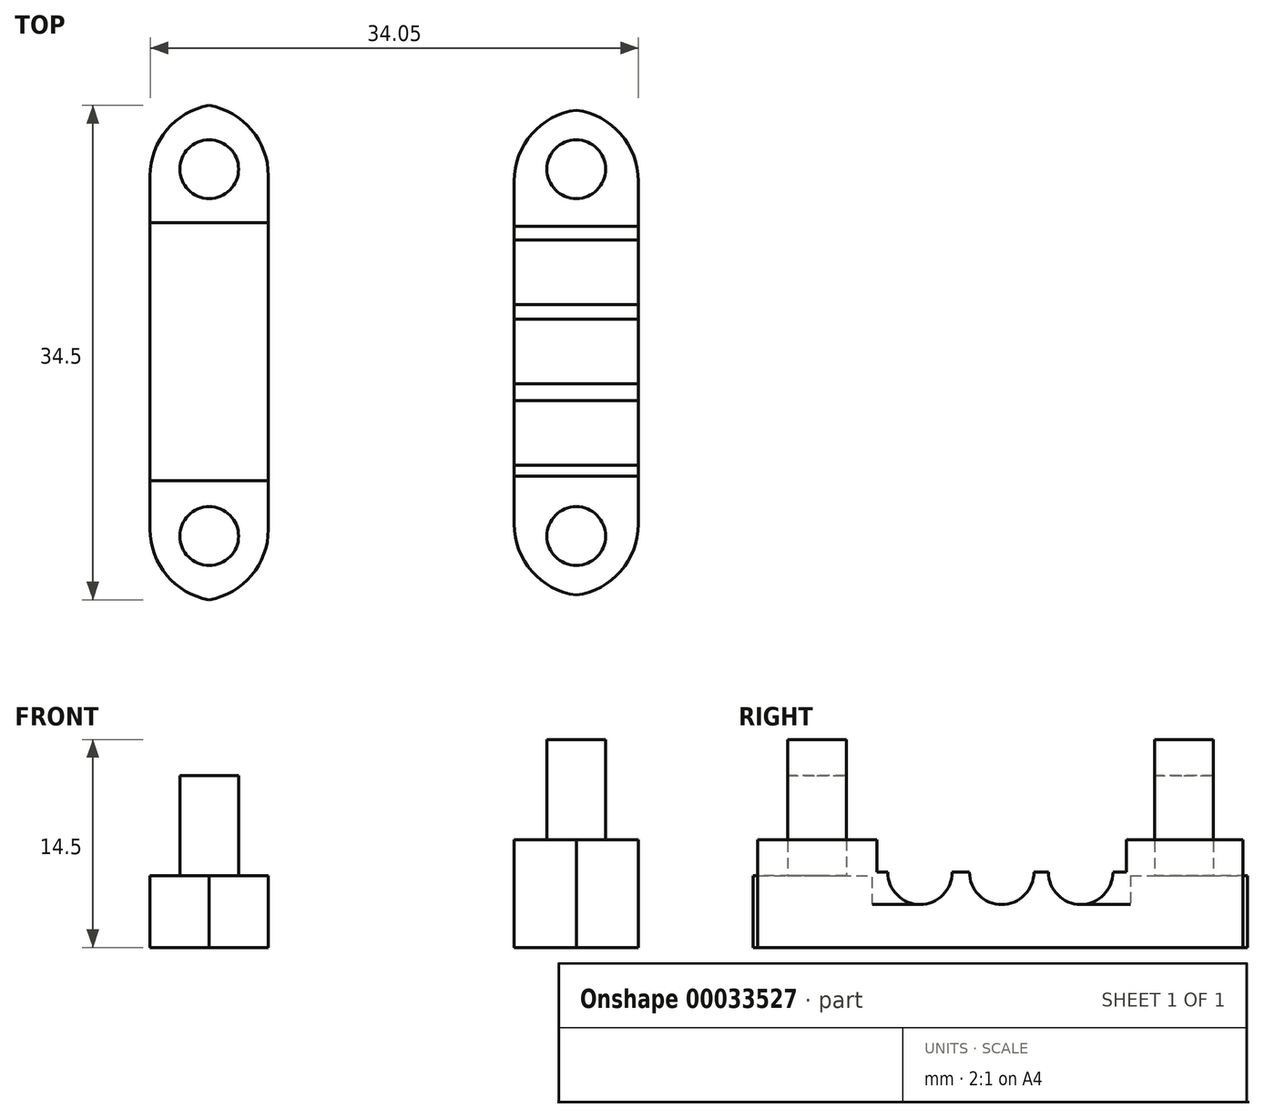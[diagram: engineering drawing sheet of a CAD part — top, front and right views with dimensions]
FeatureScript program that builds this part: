
annotation { "Feature Type Name" : "Feature", "Feature Type Description" : "" }
export const myFeature = defineFeature(function(context is Context, id is Id, definition is map)
    precondition{}
    {
        {
            var Q0;
            Q0=qCreatedBy(makeId("Top.planeOp"),FACE);
            var sketch = newSketch(context, id + "F0", { "sketchPlane" : qUnion([Q0])});
            skCircle(sketch, "E0", {"center": v(0, 0) * mm, "radius": 1.9 * mm});
            skLineSegment(sketch, "E1", {"start": v(0, 0) * mm, "end": v(0, -25.6) * mm});
            skCircle(sketch, "E2", {"center": v(0, -25.6) * mm, "radius": 1.9 * mm});
            skLineSegment(sketch, "E3.rect.bottom", {"start": v(-4.12, -30.12) * mm, "end": v(4.12, -30.12) * mm});
            skLineSegment(sketch, "E3.rect.top", {"start": v(-4.12, 4.52) * mm, "end": v(4.12, 4.52) * mm});
            skLineSegment(sketch, "E3.rect.left", {"start": v(-4.12, -30.12) * mm, "end": v(-4.12, 4.52) * mm});
            skLineSegment(sketch, "E3.rect.right", {"start": v(4.12, -30.12) * mm, "end": v(4.12, 4.52) * mm});
            skPoint(sketch, "E3.rect.middle", {"position": v(0, -12.8) * mm});
            skSolve(sketch);
        }
        {
            var Q0;
            Q0=makeQuery(id+"F0.imprint","IMPRINT",FACE,{"disambiguationData":[TD([[makeQuery(id+"F0.imprint","IMPRINT",EDGE,{"derivedFrom":sQuery(id+"F0.wireOp",EDGE,"E0")}),1.0]])]});
            var Q1;
            Q1=makeQuery(id+"F0.imprint","IMPRINT",FACE,{"disambiguationData":[TD([[makeQuery(id+"F0.imprint","IMPRINT",EDGE,{"derivedFrom":sQuery(id+"F0.wireOp",EDGE,"E2")}),1.0]])]});
            var Q2;
            Q2=makeQuery(id+"F0.imprint","IMPRINT",FACE,{"disambiguationData":[TD([[makeQuery(id+"F0.imprint","IMPRINT",EDGE,{"derivedFrom":sQuery(id+"F0.wireOp",EDGE,"E0")}),-1.0]])]});
            extrude(context, id + "F1", {"entities" : qUnion([Q0, Q1, Q2]), "depth" : 5 * mm});
        }
        {
            var Q0;
            Q0=qCreatedBy(makeId("Top.planeOp"),FACE);
            var sketch = newSketch(context, id + "F2", { "sketchPlane" : qUnion([Q0])});
            skCircle(sketch, "E4", {"center": v(0, 0) * mm, "radius": 2.05 * mm});
            skCircle(sketch, "E5", {"center": v(0, -25.6) * mm, "radius": 2.05 * mm});
            skSolve(sketch);
        }
        {
            var Q0;
            Q0 = qSketchRegion(id + "F2", true);
            extrude(context, id + "F3", {"entities" : qUnion([Q0]), "operationType" : NewBodyOperationType.ADD, "depth" : 12 * mm});
        }
        {
            var Q0;
            Q0=qCreatedBy(makeId("Right.planeOp"),FACE);
            var sketch = newSketch(context, id + "F4", { "sketchPlane" : qUnion([Q0])});
            skPoint(sketch, "E6.orphan", {"position": v(-12.73, 0) * mm});
            skLineSegment(sketch, "E7", {"start": v(-12.73, 3) * mm, "end": v(-3.73, 3) * mm});
            skLineSegment(sketch, "E8", {"start": v(-3.73, 3) * mm, "end": v(-3.73, 5) * mm});
            skLineSegment(sketch, "E9", {"start": v(-3.73, 5) * mm, "end": v(-21.73, 5) * mm});
            skLineSegment(sketch, "E10", {"start": v(-21.73, 5) * mm, "end": v(-21.73, 3) * mm});
            skLineSegment(sketch, "E11", {"start": v(-21.73, 3) * mm, "end": v(-12.73, 3) * mm});
            skSolve(sketch);
        }
        {
            var Q0;
            Q0 = qSketchRegion(id + "F4", true);
            extrude(context, id + "F5", {"entities" : qUnion([Q0]), "operationType" : NewBodyOperationType.REMOVE, "endBound" : BoundingType.SYMMETRIC, "oppositeDirection" : true, "depth" : 25 * mm});
        }
        {
            var Q0;
            Q0=makeQuery(id+"F1.opExtrude","SWEPT_EDGE",EDGE,{"disambiguationData":[OSD([sQuery(id+"F0.wireOp",EDGE,"E3.rect.top"),sQuery(id+"F0.wireOp",EDGE,"E3.rect.right")])]});
            var Q1;
            Q1=makeQuery(id+"F1.opExtrude","SWEPT_EDGE",EDGE,{"disambiguationData":[OSD([sQuery(id+"F0.wireOp",EDGE,"E3.rect.top"),sQuery(id+"F0.wireOp",EDGE,"E3.rect.left")])]});
            var Q2;
            Q2=makeQuery(id+"F1.opExtrude","SWEPT_EDGE",EDGE,{"disambiguationData":[OSD([sQuery(id+"F0.wireOp",EDGE,"E3.rect.bottom"),sQuery(id+"F0.wireOp",EDGE,"E3.rect.left")])]});
            var Q3;
            Q3=makeQuery(id+"F1.opExtrude","SWEPT_EDGE",EDGE,{"disambiguationData":[OSD([sQuery(id+"F0.wireOp",EDGE,"E3.rect.bottom"),sQuery(id+"F0.wireOp",EDGE,"E3.rect.right")])]});
            fillet(context, id + "F6", {"entities" : qUnion([Q0, Q1, Q2, Q3]), "radius" : 5 * mm, "tangentPropagation" : true, "allowEdgeOverflow" : false});
        }
        {
            var Q0;
            Q0=qCreatedBy(makeId("Top.planeOp"),FACE);
            var sketch = newSketch(context, id + "F7", { "sketchPlane" : qUnion([Q0])});
            skCircle(sketch, "E12", {"center": v(25.6, 0) * mm, "radius": 2.05 * mm});
            skCircle(sketch, "E13", {"center": v(25.6, -25.6) * mm, "radius": 2.05 * mm});
            skLineSegment(sketch, "E14.rect.bottom", {"start": v(29.93, -29.77) * mm, "end": v(21.27, -29.77) * mm});
            skLineSegment(sketch, "E14.rect.top", {"start": v(29.93, 4.17) * mm, "end": v(21.27, 4.17) * mm});
            skLineSegment(sketch, "E14.rect.left", {"start": v(29.93, -29.77) * mm, "end": v(29.93, 4.17) * mm});
            skLineSegment(sketch, "E14.rect.right", {"start": v(21.27, -29.77) * mm, "end": v(21.27, 4.17) * mm});
            skPoint(sketch, "E14.rect.middle", {"position": v(25.6, -12.8) * mm});
            skSolve(sketch);
        }
        {
            var Q0;
            Q0 = qSketchRegion(id + "F7", true);
            var Q1;
            Q1=makeQuery(id+"F7.imprint","IMPRINT",FACE,{"disambiguationData":[TD([[makeQuery(id+"F7.imprint","IMPRINT",EDGE,{"derivedFrom":sQuery(id+"F7.wireOp",EDGE,"E13")}),1.0]])]});
            var Q2;
            Q2=makeQuery(id+"F7.imprint","IMPRINT",FACE,{"disambiguationData":[TD([[makeQuery(id+"F7.imprint","IMPRINT",EDGE,{"derivedFrom":sQuery(id+"F7.wireOp",EDGE,"E12")}),1.0]])]});
            extrude(context, id + "F8", {"entities" : qUnion([Q0, Q1, Q2]), "depth" : 7.5 * mm});
        }
        {
            var Q0;
            Q0=makeQuery(id+"F7.imprint","IMPRINT",FACE,{"disambiguationData":[TD([[makeQuery(id+"F7.imprint","IMPRINT",EDGE,{"derivedFrom":sQuery(id+"F7.wireOp",EDGE,"E12")}),1.0]])]});
            var Q1;
            Q1=makeQuery(id+"F7.imprint","IMPRINT",FACE,{"disambiguationData":[TD([[makeQuery(id+"F7.imprint","IMPRINT",EDGE,{"derivedFrom":sQuery(id+"F7.wireOp",EDGE,"E13")}),1.0]])]});
            extrude(context, id + "F9", {"entities" : qUnion([Q0, Q1]), "operationType" : NewBodyOperationType.ADD, "depth" : 14.5 * mm});
        }
        {
            var Q0;
            Q0=makeQuery(id+"F8.opExtrude","SWEPT_EDGE",EDGE,{"disambiguationData":[OSD([sQuery(id+"F7.wireOp",EDGE,"E14.rect.top"),sQuery(id+"F7.wireOp",EDGE,"E14.rect.left")])]});
            var Q1;
            Q1=makeQuery(id+"F8.opExtrude","SWEPT_EDGE",EDGE,{"disambiguationData":[OSD([sQuery(id+"F7.wireOp",EDGE,"E14.rect.bottom"),sQuery(id+"F7.wireOp",EDGE,"E14.rect.left")])]});
            var Q2;
            Q2=makeQuery(id+"F8.opExtrude","SWEPT_EDGE",EDGE,{"disambiguationData":[OSD([sQuery(id+"F7.wireOp",EDGE,"E14.rect.bottom"),sQuery(id+"F7.wireOp",EDGE,"E14.rect.right")])]});
            var Q3;
            Q3=makeQuery(id+"F8.opExtrude","SWEPT_EDGE",EDGE,{"disambiguationData":[OSD([sQuery(id+"F7.wireOp",EDGE,"E14.rect.top"),sQuery(id+"F7.wireOp",EDGE,"E14.rect.right")])]});
            fillet(context, id + "F10", {"entities" : qUnion([Q0, Q1, Q2, Q3]), "radius" : 5 * mm, "tangentPropagation" : true, "allowEdgeOverflow" : false});
        }
        {
            var Q0;
            Q0=qCreatedBy(makeId("Right.planeOp"),FACE);
            var sketch = newSketch(context, id + "F11", { "sketchPlane" : qUnion([Q0])});
            skLineSegment(sketch, "E15", {"start": v(0, 0) * mm, "end": v(-4, 0) * mm});
            skLineSegment(sketch, "E16", {"start": v(-4, 0) * mm, "end": v(-4, 3) * mm});
            skLineSegment(sketch, "E17", {"start": v(-4, 3) * mm, "end": v(-4, 5.25) * mm});
            skLineSegment(sketch, "E18", {"start": v(-4, 5.25) * mm, "end": v(-4.95, 5.25) * mm});
            skArc(sketch, "E19", {"start": v(-14.96, 5.25) * mm, "mid": v(-12.71, 3) * mm, "end": v(-10.46, 5.25) * mm});
            skArc(sketch, "E20", {"start": v(-9.45, 5.25) * mm, "mid": v(-7.2, 3) * mm, "end": v(-4.95, 5.25) * mm});
            skArc(sketch, "E21", {"start": v(-20.66, 5.25) * mm, "mid": v(-18.4, 3) * mm, "end": v(-16.16, 5.25) * mm});
            skLineSegment(sketch, "E22", {"start": v(-4, 5.25) * mm, "end": v(-4, 7.5) * mm});
            skLineSegment(sketch, "E23", {"start": v(-4, 7.5) * mm, "end": v(-21.42, 7.5) * mm});
            skLineSegment(sketch, "E24", {"start": v(-21.42, 7.5) * mm, "end": v(-21.42, 5.25) * mm});
            skLineSegment(sketch, "E25.trimOffspring", {"start": v(-20.66, 5.25) * mm, "end": v(-21.42, 5.25) * mm});
            skLineSegment(sketch, "E26.trimOffspring", {"start": v(-14.96, 5.25) * mm, "end": v(-16.16, 5.25) * mm});
            skLineSegment(sketch, "E27.trimOffspring", {"start": v(-9.45, 5.25) * mm, "end": v(-10.46, 5.25) * mm});
            skSolve(sketch);
        }
        {
            var Q0;
            Q0 = qSketchRegion(id + "F11", true);
            extrude(context, id + "F12", {"entities" : qUnion([Q0]), "operationType" : NewBodyOperationType.REMOVE, "endBound" : BoundingType.THROUGH_ALL, "depth" : 25 * mm});
        }
    });
